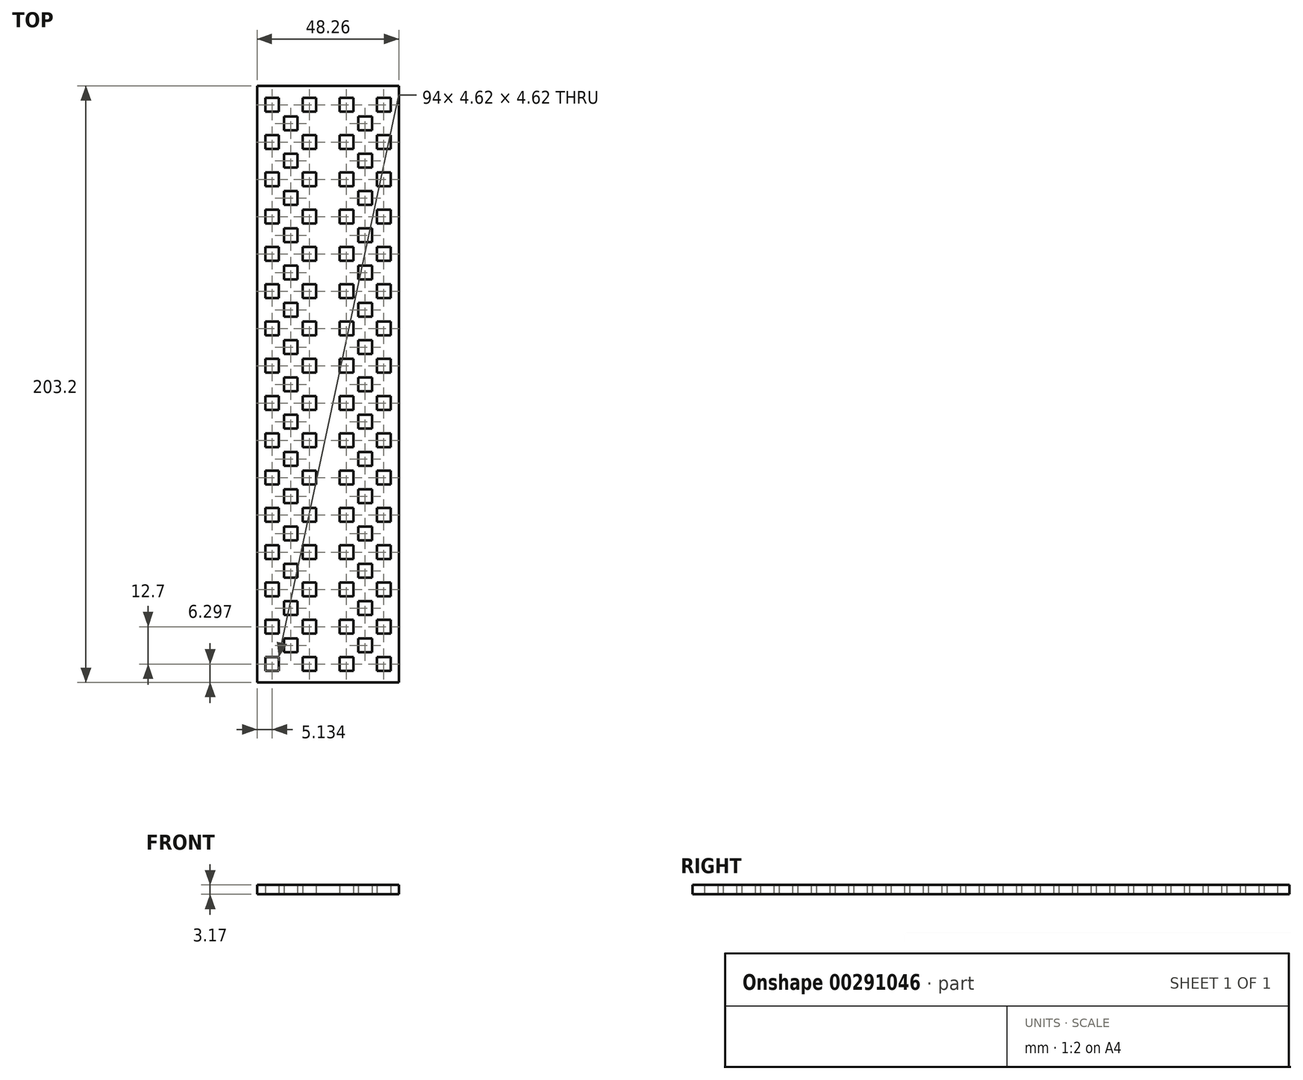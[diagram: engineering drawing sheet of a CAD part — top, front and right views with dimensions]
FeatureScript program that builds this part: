
annotation { "Feature Type Name" : "Feature", "Feature Type Description" : "" }
export const myFeature = defineFeature(function(context is Context, id is Id, definition is map)
    precondition{}
    {
        {
            var Q0;
            Q0=qCreatedBy(makeId("Top.planeOp"),FACE);
            var sketch = newSketch(context, id + "F0", { "sketchPlane" : qUnion([Q0])});
            skLineSegment(sketch, "E0.bottom", {"start": v(-11.58, 137.79) * mm, "end": v(12.55, 137.79) * mm});
            skLineSegment(sketch, "E0.top", {"start": v(-11.58, -65.41) * mm, "end": v(12.55, -65.41) * mm});
            skLineSegment(sketch, "E0.left", {"start": v(-11.58, 137.79) * mm, "end": v(-11.58, -65.41) * mm});
            skLineSegment(sketch, "E0.right", {"start": v(12.55, 137.79) * mm, "end": v(12.55, -65.41) * mm});
            skPoint(sketch, "E1", {"position": v(-7.59, 137.79) * mm});
            skPoint(sketch, "E2", {"position": v(-11.58, 133.7) * mm});
            skLineSegment(sketch, "E3.bottom", {"start": v(-7.59, 133.7) * mm, "end": v(-2.97, 133.7) * mm});
            skLineSegment(sketch, "E3.top", {"start": v(-7.59, 129.08) * mm, "end": v(-2.97, 129.08) * mm});
            skLineSegment(sketch, "E3.left", {"start": v(-7.59, 133.7) * mm, "end": v(-7.59, 129.08) * mm});
            skLineSegment(sketch, "E3.right", {"start": v(-2.97, 133.7) * mm, "end": v(-2.97, 129.08) * mm});
            skPoint(sketch, "E4", {"position": v(-5.28, 133.7) * mm});
            skPoint(sketch, "E5", {"position": v(-7.59, 131.39) * mm});
            skPoint(sketch, "E6", {"position": v(7.42, 133.7) * mm});
            skPoint(sketch, "E7", {"position": v(1.07, 133.7) * mm});
            skLineSegment(sketch, "E8.bottom", {"start": v(5.11, 133.7) * mm, "end": v(9.73, 133.7) * mm});
            skLineSegment(sketch, "E8.top", {"start": v(5.11, 129.08) * mm, "end": v(9.73, 129.08) * mm});
            skLineSegment(sketch, "E8.left", {"start": v(5.11, 133.7) * mm, "end": v(5.11, 129.08) * mm});
            skLineSegment(sketch, "E8.right", {"start": v(9.73, 133.7) * mm, "end": v(9.73, 129.08) * mm});
            skPoint(sketch, "E9", {"position": v(-7.59, 118.84) * mm});
            skPoint(sketch, "E10.0.1.0", {"position": v(7.42, 121) * mm});
            skPoint(sketch, "E10.0.1.1", {"position": v(-7.59, 118.69) * mm});
            skLineSegment(sketch, "E10.0.1.2", {"start": v(9.73, 121) * mm, "end": v(9.73, 116.38) * mm});
            skLineSegment(sketch, "E10.0.1.3", {"start": v(5.11, 121) * mm, "end": v(5.11, 116.38) * mm});
            skLineSegment(sketch, "E10.0.1.4", {"start": v(5.11, 116.38) * mm, "end": v(9.73, 116.38) * mm});
            skLineSegment(sketch, "E10.0.1.5", {"start": v(-2.97, 121) * mm, "end": v(-2.97, 116.38) * mm});
            skLineSegment(sketch, "E10.0.1.6", {"start": v(-7.59, 116.38) * mm, "end": v(-2.97, 116.38) * mm});
            skPoint(sketch, "E10.0.1.7", {"position": v(1.07, 121) * mm});
            skPoint(sketch, "E10.0.1.8", {"position": v(-5.28, 121) * mm});
            skLineSegment(sketch, "E10.0.1.9", {"start": v(5.11, 121) * mm, "end": v(9.73, 121) * mm});
            skLineSegment(sketch, "E10.0.1.10", {"start": v(-7.59, 121) * mm, "end": v(-7.59, 116.38) * mm});
            skLineSegment(sketch, "E10.0.1.11", {"start": v(-7.59, 121) * mm, "end": v(-2.97, 121) * mm});
            skPoint(sketch, "E10.0.2.0", {"position": v(7.42, 108.3) * mm});
            skPoint(sketch, "E10.0.2.1", {"position": v(-7.59, 105.99) * mm});
            skLineSegment(sketch, "E10.0.2.2", {"start": v(9.73, 108.3) * mm, "end": v(9.73, 103.68) * mm});
            skLineSegment(sketch, "E10.0.2.3", {"start": v(5.11, 108.3) * mm, "end": v(5.11, 103.68) * mm});
            skLineSegment(sketch, "E10.0.2.4", {"start": v(5.11, 103.68) * mm, "end": v(9.73, 103.68) * mm});
            skLineSegment(sketch, "E10.0.2.5", {"start": v(-2.97, 108.3) * mm, "end": v(-2.97, 103.68) * mm});
            skLineSegment(sketch, "E10.0.2.6", {"start": v(-7.59, 103.68) * mm, "end": v(-2.97, 103.68) * mm});
            skPoint(sketch, "E10.0.2.7", {"position": v(1.07, 108.3) * mm});
            skPoint(sketch, "E10.0.2.8", {"position": v(-5.28, 108.3) * mm});
            skLineSegment(sketch, "E10.0.2.9", {"start": v(5.11, 108.3) * mm, "end": v(9.73, 108.3) * mm});
            skLineSegment(sketch, "E10.0.2.10", {"start": v(-7.59, 108.3) * mm, "end": v(-7.59, 103.68) * mm});
            skLineSegment(sketch, "E10.0.2.11", {"start": v(-7.59, 108.3) * mm, "end": v(-2.97, 108.3) * mm});
            skPoint(sketch, "E10.0.3.0", {"position": v(7.42, 95.6) * mm});
            skPoint(sketch, "E10.0.3.1", {"position": v(-7.59, 93.29) * mm});
            skLineSegment(sketch, "E10.0.3.2", {"start": v(9.73, 95.6) * mm, "end": v(9.73, 90.98) * mm});
            skLineSegment(sketch, "E10.0.3.3", {"start": v(5.11, 95.6) * mm, "end": v(5.11, 90.98) * mm});
            skLineSegment(sketch, "E10.0.3.4", {"start": v(5.11, 90.98) * mm, "end": v(9.73, 90.98) * mm});
            skLineSegment(sketch, "E10.0.3.5", {"start": v(-2.97, 95.6) * mm, "end": v(-2.97, 90.98) * mm});
            skLineSegment(sketch, "E10.0.3.6", {"start": v(-7.59, 90.98) * mm, "end": v(-2.97, 90.98) * mm});
            skPoint(sketch, "E10.0.3.7", {"position": v(1.07, 95.6) * mm});
            skPoint(sketch, "E10.0.3.8", {"position": v(-5.28, 95.6) * mm});
            skLineSegment(sketch, "E10.0.3.9", {"start": v(5.11, 95.6) * mm, "end": v(9.73, 95.6) * mm});
            skLineSegment(sketch, "E10.0.3.10", {"start": v(-7.59, 95.6) * mm, "end": v(-7.59, 90.98) * mm});
            skLineSegment(sketch, "E10.0.3.11", {"start": v(-7.59, 95.6) * mm, "end": v(-2.97, 95.6) * mm});
            skPoint(sketch, "E10.0.4.0", {"position": v(7.42, 82.9) * mm});
            skPoint(sketch, "E10.0.4.1", {"position": v(-7.59, 80.59) * mm});
            skLineSegment(sketch, "E10.0.4.2", {"start": v(9.73, 82.9) * mm, "end": v(9.73, 78.28) * mm});
            skLineSegment(sketch, "E10.0.4.3", {"start": v(5.11, 82.9) * mm, "end": v(5.11, 78.28) * mm});
            skLineSegment(sketch, "E10.0.4.4", {"start": v(5.11, 78.28) * mm, "end": v(9.73, 78.28) * mm});
            skLineSegment(sketch, "E10.0.4.5", {"start": v(-2.97, 82.9) * mm, "end": v(-2.97, 78.28) * mm});
            skLineSegment(sketch, "E10.0.4.6", {"start": v(-7.59, 78.28) * mm, "end": v(-2.97, 78.28) * mm});
            skPoint(sketch, "E10.0.4.7", {"position": v(1.07, 82.9) * mm});
            skPoint(sketch, "E10.0.4.8", {"position": v(-5.28, 82.9) * mm});
            skLineSegment(sketch, "E10.0.4.9", {"start": v(5.11, 82.9) * mm, "end": v(9.73, 82.9) * mm});
            skLineSegment(sketch, "E10.0.4.10", {"start": v(-7.59, 82.9) * mm, "end": v(-7.59, 78.28) * mm});
            skLineSegment(sketch, "E10.0.4.11", {"start": v(-7.59, 82.9) * mm, "end": v(-2.97, 82.9) * mm});
            skPoint(sketch, "E10.0.5.0", {"position": v(7.42, 70.2) * mm});
            skPoint(sketch, "E10.0.5.1", {"position": v(-7.59, 67.89) * mm});
            skLineSegment(sketch, "E10.0.5.2", {"start": v(9.73, 70.2) * mm, "end": v(9.73, 65.58) * mm});
            skLineSegment(sketch, "E10.0.5.3", {"start": v(5.11, 70.2) * mm, "end": v(5.11, 65.58) * mm});
            skLineSegment(sketch, "E10.0.5.4", {"start": v(5.11, 65.58) * mm, "end": v(9.73, 65.58) * mm});
            skLineSegment(sketch, "E10.0.5.5", {"start": v(-2.97, 70.2) * mm, "end": v(-2.97, 65.58) * mm});
            skLineSegment(sketch, "E10.0.5.6", {"start": v(-7.59, 65.58) * mm, "end": v(-2.97, 65.58) * mm});
            skPoint(sketch, "E10.0.5.7", {"position": v(1.07, 70.2) * mm});
            skPoint(sketch, "E10.0.5.8", {"position": v(-5.28, 70.2) * mm});
            skLineSegment(sketch, "E10.0.5.9", {"start": v(5.11, 70.2) * mm, "end": v(9.73, 70.2) * mm});
            skLineSegment(sketch, "E10.0.5.10", {"start": v(-7.59, 70.2) * mm, "end": v(-7.59, 65.58) * mm});
            skLineSegment(sketch, "E10.0.5.11", {"start": v(-7.59, 70.2) * mm, "end": v(-2.97, 70.2) * mm});
            skPoint(sketch, "E10.0.6.0", {"position": v(7.42, 57.5) * mm});
            skPoint(sketch, "E10.0.6.1", {"position": v(-7.59, 55.19) * mm});
            skLineSegment(sketch, "E10.0.6.2", {"start": v(9.73, 57.5) * mm, "end": v(9.73, 52.88) * mm});
            skLineSegment(sketch, "E10.0.6.3", {"start": v(5.11, 57.5) * mm, "end": v(5.11, 52.88) * mm});
            skLineSegment(sketch, "E10.0.6.4", {"start": v(5.11, 52.88) * mm, "end": v(9.73, 52.88) * mm});
            skLineSegment(sketch, "E10.0.6.5", {"start": v(-2.97, 57.5) * mm, "end": v(-2.97, 52.88) * mm});
            skLineSegment(sketch, "E10.0.6.6", {"start": v(-7.59, 52.88) * mm, "end": v(-2.97, 52.88) * mm});
            skPoint(sketch, "E10.0.6.7", {"position": v(1.07, 57.5) * mm});
            skPoint(sketch, "E10.0.6.8", {"position": v(-5.28, 57.5) * mm});
            skLineSegment(sketch, "E10.0.6.9", {"start": v(5.11, 57.5) * mm, "end": v(9.73, 57.5) * mm});
            skLineSegment(sketch, "E10.0.6.10", {"start": v(-7.59, 57.5) * mm, "end": v(-7.59, 52.88) * mm});
            skLineSegment(sketch, "E10.0.6.11", {"start": v(-7.59, 57.5) * mm, "end": v(-2.97, 57.5) * mm});
            skPoint(sketch, "E10.0.7.0", {"position": v(7.42, 44.8) * mm});
            skPoint(sketch, "E10.0.7.1", {"position": v(-7.59, 42.49) * mm});
            skLineSegment(sketch, "E10.0.7.2", {"start": v(9.73, 44.8) * mm, "end": v(9.73, 40.18) * mm});
            skLineSegment(sketch, "E10.0.7.3", {"start": v(5.11, 44.8) * mm, "end": v(5.11, 40.18) * mm});
            skLineSegment(sketch, "E10.0.7.4", {"start": v(5.11, 40.18) * mm, "end": v(9.73, 40.18) * mm});
            skLineSegment(sketch, "E10.0.7.5", {"start": v(-2.97, 44.8) * mm, "end": v(-2.97, 40.18) * mm});
            skLineSegment(sketch, "E10.0.7.6", {"start": v(-7.59, 40.18) * mm, "end": v(-2.97, 40.18) * mm});
            skPoint(sketch, "E10.0.7.7", {"position": v(1.07, 44.8) * mm});
            skPoint(sketch, "E10.0.7.8", {"position": v(-5.28, 44.8) * mm});
            skLineSegment(sketch, "E10.0.7.9", {"start": v(5.11, 44.8) * mm, "end": v(9.73, 44.8) * mm});
            skLineSegment(sketch, "E10.0.7.10", {"start": v(-7.59, 44.8) * mm, "end": v(-7.59, 40.18) * mm});
            skLineSegment(sketch, "E10.0.7.11", {"start": v(-7.59, 44.8) * mm, "end": v(-2.97, 44.8) * mm});
            skPoint(sketch, "E10.0.8.0", {"position": v(7.42, 32.1) * mm});
            skPoint(sketch, "E10.0.8.1", {"position": v(-7.59, 29.79) * mm});
            skLineSegment(sketch, "E10.0.8.2", {"start": v(9.73, 32.1) * mm, "end": v(9.73, 27.48) * mm});
            skLineSegment(sketch, "E10.0.8.3", {"start": v(5.11, 32.1) * mm, "end": v(5.11, 27.48) * mm});
            skLineSegment(sketch, "E10.0.8.4", {"start": v(5.11, 27.48) * mm, "end": v(9.73, 27.48) * mm});
            skLineSegment(sketch, "E10.0.8.5", {"start": v(-2.97, 32.1) * mm, "end": v(-2.97, 27.48) * mm});
            skLineSegment(sketch, "E10.0.8.6", {"start": v(-7.59, 27.48) * mm, "end": v(-2.97, 27.48) * mm});
            skPoint(sketch, "E10.0.8.7", {"position": v(1.07, 32.1) * mm});
            skPoint(sketch, "E10.0.8.8", {"position": v(-5.28, 32.1) * mm});
            skLineSegment(sketch, "E10.0.8.9", {"start": v(5.11, 32.1) * mm, "end": v(9.73, 32.1) * mm});
            skLineSegment(sketch, "E10.0.8.10", {"start": v(-7.59, 32.1) * mm, "end": v(-7.59, 27.48) * mm});
            skLineSegment(sketch, "E10.0.8.11", {"start": v(-7.59, 32.1) * mm, "end": v(-2.97, 32.1) * mm});
            skPoint(sketch, "E10.0.9.0", {"position": v(7.42, 19.4) * mm});
            skPoint(sketch, "E10.0.9.1", {"position": v(-7.59, 17.09) * mm});
            skLineSegment(sketch, "E10.0.9.2", {"start": v(9.73, 19.4) * mm, "end": v(9.73, 14.78) * mm});
            skLineSegment(sketch, "E10.0.9.3", {"start": v(5.11, 19.4) * mm, "end": v(5.11, 14.78) * mm});
            skLineSegment(sketch, "E10.0.9.4", {"start": v(5.11, 14.78) * mm, "end": v(9.73, 14.78) * mm});
            skLineSegment(sketch, "E10.0.9.5", {"start": v(-2.97, 19.4) * mm, "end": v(-2.97, 14.78) * mm});
            skLineSegment(sketch, "E10.0.9.6", {"start": v(-7.59, 14.78) * mm, "end": v(-2.97, 14.78) * mm});
            skPoint(sketch, "E10.0.9.7", {"position": v(1.07, 19.4) * mm});
            skPoint(sketch, "E10.0.9.8", {"position": v(-5.28, 19.4) * mm});
            skLineSegment(sketch, "E10.0.9.9", {"start": v(5.11, 19.4) * mm, "end": v(9.73, 19.4) * mm});
            skLineSegment(sketch, "E10.0.9.10", {"start": v(-7.59, 19.4) * mm, "end": v(-7.59, 14.78) * mm});
            skLineSegment(sketch, "E10.0.9.11", {"start": v(-7.59, 19.4) * mm, "end": v(-2.97, 19.4) * mm});
            skPoint(sketch, "E10.0.10.0", {"position": v(7.42, 6.7) * mm});
            skPoint(sketch, "E10.0.10.1", {"position": v(-7.59, 4.39) * mm});
            skLineSegment(sketch, "E10.0.10.2", {"start": v(9.73, 6.7) * mm, "end": v(9.73, 2.08) * mm});
            skLineSegment(sketch, "E10.0.10.3", {"start": v(5.11, 6.7) * mm, "end": v(5.11, 2.08) * mm});
            skLineSegment(sketch, "E10.0.10.4", {"start": v(5.11, 2.08) * mm, "end": v(9.73, 2.08) * mm});
            skLineSegment(sketch, "E10.0.10.5", {"start": v(-2.97, 6.7) * mm, "end": v(-2.97, 2.08) * mm});
            skLineSegment(sketch, "E10.0.10.6", {"start": v(-7.59, 2.08) * mm, "end": v(-2.97, 2.08) * mm});
            skPoint(sketch, "E10.0.10.7", {"position": v(1.07, 6.7) * mm});
            skPoint(sketch, "E10.0.10.8", {"position": v(-5.28, 6.7) * mm});
            skLineSegment(sketch, "E10.0.10.9", {"start": v(5.11, 6.7) * mm, "end": v(9.73, 6.7) * mm});
            skLineSegment(sketch, "E10.0.10.10", {"start": v(-7.59, 6.7) * mm, "end": v(-7.59, 2.08) * mm});
            skLineSegment(sketch, "E10.0.10.11", {"start": v(-7.59, 6.7) * mm, "end": v(-2.97, 6.7) * mm});
            skPoint(sketch, "E10.0.11.0", {"position": v(7.42, -6) * mm});
            skPoint(sketch, "E10.0.11.1", {"position": v(-7.59, -8.31) * mm});
            skLineSegment(sketch, "E10.0.11.2", {"start": v(9.73, -6) * mm, "end": v(9.73, -10.62) * mm});
            skLineSegment(sketch, "E10.0.11.3", {"start": v(5.11, -6) * mm, "end": v(5.11, -10.62) * mm});
            skLineSegment(sketch, "E10.0.11.4", {"start": v(5.11, -10.62) * mm, "end": v(9.73, -10.62) * mm});
            skLineSegment(sketch, "E10.0.11.5", {"start": v(-2.97, -6) * mm, "end": v(-2.97, -10.62) * mm});
            skLineSegment(sketch, "E10.0.11.6", {"start": v(-7.59, -10.62) * mm, "end": v(-2.97, -10.62) * mm});
            skPoint(sketch, "E10.0.11.7", {"position": v(1.07, -6) * mm});
            skPoint(sketch, "E10.0.11.8", {"position": v(-5.28, -6) * mm});
            skLineSegment(sketch, "E10.0.11.9", {"start": v(5.11, -6) * mm, "end": v(9.73, -6) * mm});
            skLineSegment(sketch, "E10.0.11.10", {"start": v(-7.59, -6) * mm, "end": v(-7.59, -10.62) * mm});
            skLineSegment(sketch, "E10.0.11.11", {"start": v(-7.59, -6) * mm, "end": v(-2.97, -6) * mm});
            skPoint(sketch, "E10.0.12.0", {"position": v(7.42, -18.7) * mm});
            skPoint(sketch, "E10.0.12.1", {"position": v(-7.59, -21.01) * mm});
            skLineSegment(sketch, "E10.0.12.2", {"start": v(9.73, -18.7) * mm, "end": v(9.73, -23.32) * mm});
            skLineSegment(sketch, "E10.0.12.3", {"start": v(5.11, -18.7) * mm, "end": v(5.11, -23.32) * mm});
            skLineSegment(sketch, "E10.0.12.4", {"start": v(5.11, -23.32) * mm, "end": v(9.73, -23.32) * mm});
            skLineSegment(sketch, "E10.0.12.5", {"start": v(-2.97, -18.7) * mm, "end": v(-2.97, -23.32) * mm});
            skLineSegment(sketch, "E10.0.12.6", {"start": v(-7.59, -23.32) * mm, "end": v(-2.97, -23.32) * mm});
            skPoint(sketch, "E10.0.12.7", {"position": v(1.07, -18.7) * mm});
            skPoint(sketch, "E10.0.12.8", {"position": v(-5.28, -18.7) * mm});
            skLineSegment(sketch, "E10.0.12.9", {"start": v(5.11, -18.7) * mm, "end": v(9.73, -18.7) * mm});
            skLineSegment(sketch, "E10.0.12.10", {"start": v(-7.59, -18.7) * mm, "end": v(-7.59, -23.32) * mm});
            skLineSegment(sketch, "E10.0.12.11", {"start": v(-7.59, -18.7) * mm, "end": v(-2.97, -18.7) * mm});
            skPoint(sketch, "E10.0.13.0", {"position": v(7.42, -31.4) * mm});
            skPoint(sketch, "E10.0.13.1", {"position": v(-7.59, -33.71) * mm});
            skLineSegment(sketch, "E10.0.13.2", {"start": v(9.73, -31.4) * mm, "end": v(9.73, -36.02) * mm});
            skLineSegment(sketch, "E10.0.13.3", {"start": v(5.11, -31.4) * mm, "end": v(5.11, -36.02) * mm});
            skLineSegment(sketch, "E10.0.13.4", {"start": v(5.11, -36.02) * mm, "end": v(9.73, -36.02) * mm});
            skLineSegment(sketch, "E10.0.13.5", {"start": v(-2.97, -31.4) * mm, "end": v(-2.97, -36.02) * mm});
            skLineSegment(sketch, "E10.0.13.6", {"start": v(-7.59, -36.02) * mm, "end": v(-2.97, -36.02) * mm});
            skPoint(sketch, "E10.0.13.7", {"position": v(1.07, -31.4) * mm});
            skPoint(sketch, "E10.0.13.8", {"position": v(-5.28, -31.4) * mm});
            skLineSegment(sketch, "E10.0.13.9", {"start": v(5.11, -31.4) * mm, "end": v(9.73, -31.4) * mm});
            skLineSegment(sketch, "E10.0.13.10", {"start": v(-7.59, -31.4) * mm, "end": v(-7.59, -36.02) * mm});
            skLineSegment(sketch, "E10.0.13.11", {"start": v(-7.59, -31.4) * mm, "end": v(-2.97, -31.4) * mm});
            skPoint(sketch, "E10.0.14.0", {"position": v(7.42, -44.1) * mm});
            skPoint(sketch, "E10.0.14.1", {"position": v(-7.59, -46.41) * mm});
            skLineSegment(sketch, "E10.0.14.2", {"start": v(9.73, -44.1) * mm, "end": v(9.73, -48.72) * mm});
            skLineSegment(sketch, "E10.0.14.3", {"start": v(5.11, -44.1) * mm, "end": v(5.11, -48.72) * mm});
            skLineSegment(sketch, "E10.0.14.4", {"start": v(5.11, -48.72) * mm, "end": v(9.73, -48.72) * mm});
            skLineSegment(sketch, "E10.0.14.5", {"start": v(-2.97, -44.1) * mm, "end": v(-2.97, -48.72) * mm});
            skLineSegment(sketch, "E10.0.14.6", {"start": v(-7.59, -48.72) * mm, "end": v(-2.97, -48.72) * mm});
            skPoint(sketch, "E10.0.14.7", {"position": v(1.07, -44.1) * mm});
            skPoint(sketch, "E10.0.14.8", {"position": v(-5.28, -44.1) * mm});
            skLineSegment(sketch, "E10.0.14.9", {"start": v(5.11, -44.1) * mm, "end": v(9.73, -44.1) * mm});
            skLineSegment(sketch, "E10.0.14.10", {"start": v(-7.59, -44.1) * mm, "end": v(-7.59, -48.72) * mm});
            skLineSegment(sketch, "E10.0.14.11", {"start": v(-7.59, -44.1) * mm, "end": v(-2.97, -44.1) * mm});
            skPoint(sketch, "E10.0.15.0", {"position": v(7.42, -56.8) * mm});
            skPoint(sketch, "E10.0.15.1", {"position": v(-7.59, -59.11) * mm});
            skLineSegment(sketch, "E10.0.15.2", {"start": v(9.73, -56.8) * mm, "end": v(9.73, -61.42) * mm});
            skLineSegment(sketch, "E10.0.15.3", {"start": v(5.11, -56.8) * mm, "end": v(5.11, -61.42) * mm});
            skLineSegment(sketch, "E10.0.15.4", {"start": v(5.11, -61.42) * mm, "end": v(9.73, -61.42) * mm});
            skLineSegment(sketch, "E10.0.15.5", {"start": v(-2.97, -56.8) * mm, "end": v(-2.97, -61.42) * mm});
            skLineSegment(sketch, "E10.0.15.6", {"start": v(-7.59, -61.42) * mm, "end": v(-2.97, -61.42) * mm});
            skPoint(sketch, "E10.0.15.7", {"position": v(1.07, -56.8) * mm});
            skPoint(sketch, "E10.0.15.8", {"position": v(-5.28, -56.8) * mm});
            skLineSegment(sketch, "E10.0.15.9", {"start": v(5.11, -56.8) * mm, "end": v(9.73, -56.8) * mm});
            skLineSegment(sketch, "E10.0.15.10", {"start": v(-7.59, -56.8) * mm, "end": v(-7.59, -61.42) * mm});
            skLineSegment(sketch, "E10.0.15.11", {"start": v(-7.59, -56.8) * mm, "end": v(-2.97, -56.8) * mm});
            skLineSegment(sketch, "E10.direction1", {"start": v(-7.59, 131.39) * mm, "end": v(17.81, 131.39) * mm, "construction": true});
            skLineSegment(sketch, "E10.direction2", {"start": v(-7.59, 131.39) * mm, "end": v(-7.59, 118.69) * mm, "construction": true});
            skPoint(sketch, "E11", {"position": v(1.07, 127.35) * mm});
            skLineSegment(sketch, "E12.bottom", {"start": v(-1.24, 127.35) * mm, "end": v(3.38, 127.35) * mm});
            skLineSegment(sketch, "E12.top", {"start": v(-1.24, 122.73) * mm, "end": v(3.38, 122.73) * mm});
            skLineSegment(sketch, "E12.left", {"start": v(-1.24, 127.35) * mm, "end": v(-1.24, 122.73) * mm});
            skLineSegment(sketch, "E12.right", {"start": v(3.38, 127.35) * mm, "end": v(3.38, 122.73) * mm});
            skLineSegment(sketch, "E13.0.1.0", {"start": v(3.38, 114.65) * mm, "end": v(3.38, 110.03) * mm});
            skLineSegment(sketch, "E13.0.1.1", {"start": v(-1.24, 114.65) * mm, "end": v(-1.24, 110.03) * mm});
            skLineSegment(sketch, "E13.0.1.2", {"start": v(-1.24, 110.03) * mm, "end": v(3.38, 110.03) * mm});
            skPoint(sketch, "E13.0.1.3", {"position": v(1.07, 114.65) * mm});
            skLineSegment(sketch, "E13.0.1.4", {"start": v(-1.24, 114.65) * mm, "end": v(3.38, 114.65) * mm});
            skLineSegment(sketch, "E13.0.2.0", {"start": v(3.38, 101.95) * mm, "end": v(3.38, 97.33) * mm});
            skLineSegment(sketch, "E13.0.2.1", {"start": v(-1.24, 101.95) * mm, "end": v(-1.24, 97.33) * mm});
            skLineSegment(sketch, "E13.0.2.2", {"start": v(-1.24, 97.33) * mm, "end": v(3.38, 97.33) * mm});
            skPoint(sketch, "E13.0.2.3", {"position": v(1.07, 101.95) * mm});
            skLineSegment(sketch, "E13.0.2.4", {"start": v(-1.24, 101.95) * mm, "end": v(3.38, 101.95) * mm});
            skLineSegment(sketch, "E13.0.3.0", {"start": v(3.38, 89.25) * mm, "end": v(3.38, 84.63) * mm});
            skLineSegment(sketch, "E13.0.3.1", {"start": v(-1.24, 89.25) * mm, "end": v(-1.24, 84.63) * mm});
            skLineSegment(sketch, "E13.0.3.2", {"start": v(-1.24, 84.63) * mm, "end": v(3.38, 84.63) * mm});
            skPoint(sketch, "E13.0.3.3", {"position": v(1.07, 89.25) * mm});
            skLineSegment(sketch, "E13.0.3.4", {"start": v(-1.24, 89.25) * mm, "end": v(3.38, 89.25) * mm});
            skLineSegment(sketch, "E13.0.4.0", {"start": v(3.38, 76.55) * mm, "end": v(3.38, 71.93) * mm});
            skLineSegment(sketch, "E13.0.4.1", {"start": v(-1.24, 76.55) * mm, "end": v(-1.24, 71.93) * mm});
            skLineSegment(sketch, "E13.0.4.2", {"start": v(-1.24, 71.93) * mm, "end": v(3.38, 71.93) * mm});
            skPoint(sketch, "E13.0.4.3", {"position": v(1.07, 76.55) * mm});
            skLineSegment(sketch, "E13.0.4.4", {"start": v(-1.24, 76.55) * mm, "end": v(3.38, 76.55) * mm});
            skLineSegment(sketch, "E13.0.5.0", {"start": v(3.38, 63.85) * mm, "end": v(3.38, 59.23) * mm});
            skLineSegment(sketch, "E13.0.5.1", {"start": v(-1.24, 63.85) * mm, "end": v(-1.24, 59.23) * mm});
            skLineSegment(sketch, "E13.0.5.2", {"start": v(-1.24, 59.23) * mm, "end": v(3.38, 59.23) * mm});
            skPoint(sketch, "E13.0.5.3", {"position": v(1.07, 63.85) * mm});
            skLineSegment(sketch, "E13.0.5.4", {"start": v(-1.24, 63.85) * mm, "end": v(3.38, 63.85) * mm});
            skLineSegment(sketch, "E13.0.6.0", {"start": v(3.38, 51.15) * mm, "end": v(3.38, 46.53) * mm});
            skLineSegment(sketch, "E13.0.6.1", {"start": v(-1.24, 51.15) * mm, "end": v(-1.24, 46.53) * mm});
            skLineSegment(sketch, "E13.0.6.2", {"start": v(-1.24, 46.53) * mm, "end": v(3.38, 46.53) * mm});
            skPoint(sketch, "E13.0.6.3", {"position": v(1.07, 51.15) * mm});
            skLineSegment(sketch, "E13.0.6.4", {"start": v(-1.24, 51.15) * mm, "end": v(3.38, 51.15) * mm});
            skLineSegment(sketch, "E13.0.7.0", {"start": v(3.38, 38.45) * mm, "end": v(3.38, 33.83) * mm});
            skLineSegment(sketch, "E13.0.7.1", {"start": v(-1.24, 38.45) * mm, "end": v(-1.24, 33.83) * mm});
            skLineSegment(sketch, "E13.0.7.2", {"start": v(-1.24, 33.83) * mm, "end": v(3.38, 33.83) * mm});
            skPoint(sketch, "E13.0.7.3", {"position": v(1.07, 38.45) * mm});
            skLineSegment(sketch, "E13.0.7.4", {"start": v(-1.24, 38.45) * mm, "end": v(3.38, 38.45) * mm});
            skLineSegment(sketch, "E13.0.8.0", {"start": v(3.38, 25.75) * mm, "end": v(3.38, 21.13) * mm});
            skLineSegment(sketch, "E13.0.8.1", {"start": v(-1.24, 25.75) * mm, "end": v(-1.24, 21.13) * mm});
            skLineSegment(sketch, "E13.0.8.2", {"start": v(-1.24, 21.13) * mm, "end": v(3.38, 21.13) * mm});
            skPoint(sketch, "E13.0.8.3", {"position": v(1.07, 25.75) * mm});
            skLineSegment(sketch, "E13.0.8.4", {"start": v(-1.24, 25.75) * mm, "end": v(3.38, 25.75) * mm});
            skLineSegment(sketch, "E13.0.9.0", {"start": v(3.38, 13.05) * mm, "end": v(3.38, 8.43) * mm});
            skLineSegment(sketch, "E13.0.9.1", {"start": v(-1.24, 13.05) * mm, "end": v(-1.24, 8.43) * mm});
            skLineSegment(sketch, "E13.0.9.2", {"start": v(-1.24, 8.43) * mm, "end": v(3.38, 8.43) * mm});
            skPoint(sketch, "E13.0.9.3", {"position": v(1.07, 13.05) * mm});
            skLineSegment(sketch, "E13.0.9.4", {"start": v(-1.24, 13.05) * mm, "end": v(3.38, 13.05) * mm});
            skLineSegment(sketch, "E13.0.10.0", {"start": v(3.38, 0.35) * mm, "end": v(3.38, -4.27) * mm});
            skLineSegment(sketch, "E13.0.10.1", {"start": v(-1.24, 0.35) * mm, "end": v(-1.24, -4.27) * mm});
            skLineSegment(sketch, "E13.0.10.2", {"start": v(-1.24, -4.27) * mm, "end": v(3.38, -4.27) * mm});
            skPoint(sketch, "E13.0.10.3", {"position": v(1.07, 0.35) * mm});
            skLineSegment(sketch, "E13.0.10.4", {"start": v(-1.24, 0.35) * mm, "end": v(3.38, 0.35) * mm});
            skLineSegment(sketch, "E13.0.11.0", {"start": v(3.38, -12.35) * mm, "end": v(3.38, -16.97) * mm});
            skLineSegment(sketch, "E13.0.11.1", {"start": v(-1.24, -12.35) * mm, "end": v(-1.24, -16.97) * mm});
            skLineSegment(sketch, "E13.0.11.2", {"start": v(-1.24, -16.97) * mm, "end": v(3.38, -16.97) * mm});
            skPoint(sketch, "E13.0.11.3", {"position": v(1.07, -12.35) * mm});
            skLineSegment(sketch, "E13.0.11.4", {"start": v(-1.24, -12.35) * mm, "end": v(3.38, -12.35) * mm});
            skLineSegment(sketch, "E13.0.12.0", {"start": v(3.38, -25.05) * mm, "end": v(3.38, -29.67) * mm});
            skLineSegment(sketch, "E13.0.12.1", {"start": v(-1.24, -25.05) * mm, "end": v(-1.24, -29.67) * mm});
            skLineSegment(sketch, "E13.0.12.2", {"start": v(-1.24, -29.67) * mm, "end": v(3.38, -29.67) * mm});
            skPoint(sketch, "E13.0.12.3", {"position": v(1.07, -25.05) * mm});
            skLineSegment(sketch, "E13.0.12.4", {"start": v(-1.24, -25.05) * mm, "end": v(3.38, -25.05) * mm});
            skLineSegment(sketch, "E13.0.13.0", {"start": v(3.38, -37.75) * mm, "end": v(3.38, -42.37) * mm});
            skLineSegment(sketch, "E13.0.13.1", {"start": v(-1.24, -37.75) * mm, "end": v(-1.24, -42.37) * mm});
            skLineSegment(sketch, "E13.0.13.2", {"start": v(-1.24, -42.37) * mm, "end": v(3.38, -42.37) * mm});
            skPoint(sketch, "E13.0.13.3", {"position": v(1.07, -37.75) * mm});
            skLineSegment(sketch, "E13.0.13.4", {"start": v(-1.24, -37.75) * mm, "end": v(3.38, -37.75) * mm});
            skLineSegment(sketch, "E13.0.14.0", {"start": v(3.38, -50.45) * mm, "end": v(3.38, -55.07) * mm});
            skLineSegment(sketch, "E13.0.14.1", {"start": v(-1.24, -50.45) * mm, "end": v(-1.24, -55.07) * mm});
            skLineSegment(sketch, "E13.0.14.2", {"start": v(-1.24, -55.07) * mm, "end": v(3.38, -55.07) * mm});
            skPoint(sketch, "E13.0.14.3", {"position": v(1.07, -50.45) * mm});
            skLineSegment(sketch, "E13.0.14.4", {"start": v(-1.24, -50.45) * mm, "end": v(3.38, -50.45) * mm});
            skLineSegment(sketch, "E13.direction1", {"start": v(-1.24, 122.73) * mm, "end": v(24.16, 122.73) * mm, "construction": true});
            skLineSegment(sketch, "E13.direction2", {"start": v(-1.24, 122.73) * mm, "end": v(-1.24, 110.03) * mm, "construction": true});
            skSolve(sketch);
        }
        {
            var Q0;
            Q0=makeQuery(id+"F0.imprint","IMPRINT",FACE,{"disambiguationData":[TD([[makeQuery(id+"F0.imprint","IMPRINT",EDGE,{"derivedFrom":sQuery(id+"F0.wireOp",EDGE,"E0.bottom")}),-1.0]])]});
            extrude(context, id + "F1", {"entities" : qUnion([Q0]), "depth" : 3.17 * mm});
        }
        {
            var Q0;
            Q0=makeQuery(id+"F1.opExtrude","SWEPT_BODY",BODY,{"disambiguationData":[OSD([sQuery(id+"F0.wireOp",EDGE,"E0.bottom"),sQuery(id+"F0.wireOp",EDGE,"E0.top"),sQuery(id+"F0.wireOp",EDGE,"E0.left"),sQuery(id+"F0.wireOp",EDGE,"E0.right"),sQuery(id+"F0.wireOp",EDGE,"E3.bottom"),sQuery(id+"F0.wireOp",EDGE,"E3.top"),sQuery(id+"F0.wireOp",EDGE,"E3.left"),sQuery(id+"F0.wireOp",EDGE,"E3.right"),sQuery(id+"F0.wireOp",EDGE,"E8.bottom"),sQuery(id+"F0.wireOp",EDGE,"E8.top"),sQuery(id+"F0.wireOp",EDGE,"E8.left"),sQuery(id+"F0.wireOp",EDGE,"E8.right"),sQuery(id+"F0.wireOp",EDGE,"E10.0.1.2"),sQuery(id+"F0.wireOp",EDGE,"E10.0.1.3"),sQuery(id+"F0.wireOp",EDGE,"E10.0.1.4"),sQuery(id+"F0.wireOp",EDGE,"E10.0.1.5"),sQuery(id+"F0.wireOp",EDGE,"E10.0.1.6"),sQuery(id+"F0.wireOp",EDGE,"E10.0.1.9"),sQuery(id+"F0.wireOp",EDGE,"E10.0.1.10"),sQuery(id+"F0.wireOp",EDGE,"E10.0.1.11"),sQuery(id+"F0.wireOp",EDGE,"E10.0.2.2"),sQuery(id+"F0.wireOp",EDGE,"E10.0.2.3"),sQuery(id+"F0.wireOp",EDGE,"E10.0.2.4"),sQuery(id+"F0.wireOp",EDGE,"E10.0.2.5"),sQuery(id+"F0.wireOp",EDGE,"E10.0.2.6"),sQuery(id+"F0.wireOp",EDGE,"E10.0.2.9"),sQuery(id+"F0.wireOp",EDGE,"E10.0.2.10"),sQuery(id+"F0.wireOp",EDGE,"E10.0.2.11"),sQuery(id+"F0.wireOp",EDGE,"E10.0.3.2"),sQuery(id+"F0.wireOp",EDGE,"E10.0.3.3"),sQuery(id+"F0.wireOp",EDGE,"E10.0.3.4"),sQuery(id+"F0.wireOp",EDGE,"E10.0.3.5"),sQuery(id+"F0.wireOp",EDGE,"E10.0.3.6"),sQuery(id+"F0.wireOp",EDGE,"E10.0.3.9"),sQuery(id+"F0.wireOp",EDGE,"E10.0.3.10"),sQuery(id+"F0.wireOp",EDGE,"E10.0.3.11"),sQuery(id+"F0.wireOp",EDGE,"E10.0.4.2"),sQuery(id+"F0.wireOp",EDGE,"E10.0.4.3"),sQuery(id+"F0.wireOp",EDGE,"E10.0.4.4"),sQuery(id+"F0.wireOp",EDGE,"E10.0.4.5"),sQuery(id+"F0.wireOp",EDGE,"E10.0.4.6"),sQuery(id+"F0.wireOp",EDGE,"E10.0.4.9"),sQuery(id+"F0.wireOp",EDGE,"E10.0.4.10"),sQuery(id+"F0.wireOp",EDGE,"E10.0.4.11"),sQuery(id+"F0.wireOp",EDGE,"E10.0.5.2"),sQuery(id+"F0.wireOp",EDGE,"E10.0.5.3"),sQuery(id+"F0.wireOp",EDGE,"E10.0.5.4"),sQuery(id+"F0.wireOp",EDGE,"E10.0.5.5"),sQuery(id+"F0.wireOp",EDGE,"E10.0.5.6"),sQuery(id+"F0.wireOp",EDGE,"E10.0.5.9"),sQuery(id+"F0.wireOp",EDGE,"E10.0.5.10"),sQuery(id+"F0.wireOp",EDGE,"E10.0.5.11"),sQuery(id+"F0.wireOp",EDGE,"E10.0.6.2"),sQuery(id+"F0.wireOp",EDGE,"E10.0.6.3"),sQuery(id+"F0.wireOp",EDGE,"E10.0.6.4"),sQuery(id+"F0.wireOp",EDGE,"E10.0.6.5"),sQuery(id+"F0.wireOp",EDGE,"E10.0.6.6"),sQuery(id+"F0.wireOp",EDGE,"E10.0.6.9"),sQuery(id+"F0.wireOp",EDGE,"E10.0.6.10"),sQuery(id+"F0.wireOp",EDGE,"E10.0.6.11"),sQuery(id+"F0.wireOp",EDGE,"E10.0.7.2"),sQuery(id+"F0.wireOp",EDGE,"E10.0.7.3"),sQuery(id+"F0.wireOp",EDGE,"E10.0.7.4"),sQuery(id+"F0.wireOp",EDGE,"E10.0.7.5"),sQuery(id+"F0.wireOp",EDGE,"E10.0.7.6"),sQuery(id+"F0.wireOp",EDGE,"E10.0.7.9"),sQuery(id+"F0.wireOp",EDGE,"E10.0.7.10"),sQuery(id+"F0.wireOp",EDGE,"E10.0.7.11"),sQuery(id+"F0.wireOp",EDGE,"E10.0.8.2"),sQuery(id+"F0.wireOp",EDGE,"E10.0.8.3"),sQuery(id+"F0.wireOp",EDGE,"E10.0.8.4"),sQuery(id+"F0.wireOp",EDGE,"E10.0.8.5"),sQuery(id+"F0.wireOp",EDGE,"E10.0.8.6"),sQuery(id+"F0.wireOp",EDGE,"E10.0.8.9"),sQuery(id+"F0.wireOp",EDGE,"E10.0.8.10"),sQuery(id+"F0.wireOp",EDGE,"E10.0.8.11"),sQuery(id+"F0.wireOp",EDGE,"E10.0.9.2"),sQuery(id+"F0.wireOp",EDGE,"E10.0.9.3"),sQuery(id+"F0.wireOp",EDGE,"E10.0.9.4"),sQuery(id+"F0.wireOp",EDGE,"E10.0.9.5"),sQuery(id+"F0.wireOp",EDGE,"E10.0.9.6"),sQuery(id+"F0.wireOp",EDGE,"E10.0.9.9"),sQuery(id+"F0.wireOp",EDGE,"E10.0.9.10"),sQuery(id+"F0.wireOp",EDGE,"E10.0.9.11"),sQuery(id+"F0.wireOp",EDGE,"E10.0.10.2"),sQuery(id+"F0.wireOp",EDGE,"E10.0.10.3"),sQuery(id+"F0.wireOp",EDGE,"E10.0.10.4"),sQuery(id+"F0.wireOp",EDGE,"E10.0.10.5"),sQuery(id+"F0.wireOp",EDGE,"E10.0.10.6"),sQuery(id+"F0.wireOp",EDGE,"E10.0.10.9"),sQuery(id+"F0.wireOp",EDGE,"E10.0.10.10"),sQuery(id+"F0.wireOp",EDGE,"E10.0.10.11"),sQuery(id+"F0.wireOp",EDGE,"E10.0.11.2"),sQuery(id+"F0.wireOp",EDGE,"E10.0.11.3"),sQuery(id+"F0.wireOp",EDGE,"E10.0.11.4"),sQuery(id+"F0.wireOp",EDGE,"E10.0.11.5"),sQuery(id+"F0.wireOp",EDGE,"E10.0.11.6"),sQuery(id+"F0.wireOp",EDGE,"E10.0.11.9"),sQuery(id+"F0.wireOp",EDGE,"E10.0.11.10"),sQuery(id+"F0.wireOp",EDGE,"E10.0.11.11"),sQuery(id+"F0.wireOp",EDGE,"E10.0.12.2"),sQuery(id+"F0.wireOp",EDGE,"E10.0.12.3"),sQuery(id+"F0.wireOp",EDGE,"E10.0.12.4"),sQuery(id+"F0.wireOp",EDGE,"E10.0.12.5"),sQuery(id+"F0.wireOp",EDGE,"E10.0.12.6"),sQuery(id+"F0.wireOp",EDGE,"E10.0.12.9"),sQuery(id+"F0.wireOp",EDGE,"E10.0.12.10"),sQuery(id+"F0.wireOp",EDGE,"E10.0.12.11"),sQuery(id+"F0.wireOp",EDGE,"E10.0.13.2"),sQuery(id+"F0.wireOp",EDGE,"E10.0.13.3"),sQuery(id+"F0.wireOp",EDGE,"E10.0.13.4"),sQuery(id+"F0.wireOp",EDGE,"E10.0.13.5"),sQuery(id+"F0.wireOp",EDGE,"E10.0.13.6"),sQuery(id+"F0.wireOp",EDGE,"E10.0.13.9"),sQuery(id+"F0.wireOp",EDGE,"E10.0.13.10"),sQuery(id+"F0.wireOp",EDGE,"E10.0.13.11"),sQuery(id+"F0.wireOp",EDGE,"E10.0.14.2"),sQuery(id+"F0.wireOp",EDGE,"E10.0.14.3"),sQuery(id+"F0.wireOp",EDGE,"E10.0.14.4"),sQuery(id+"F0.wireOp",EDGE,"E10.0.14.5"),sQuery(id+"F0.wireOp",EDGE,"E10.0.14.6"),sQuery(id+"F0.wireOp",EDGE,"E10.0.14.9"),sQuery(id+"F0.wireOp",EDGE,"E10.0.14.10"),sQuery(id+"F0.wireOp",EDGE,"E10.0.14.11"),sQuery(id+"F0.wireOp",EDGE,"E10.0.15.2"),sQuery(id+"F0.wireOp",EDGE,"E10.0.15.3"),sQuery(id+"F0.wireOp",EDGE,"E10.0.15.4"),sQuery(id+"F0.wireOp",EDGE,"E10.0.15.5"),sQuery(id+"F0.wireOp",EDGE,"E10.0.15.6"),sQuery(id+"F0.wireOp",EDGE,"E10.0.15.9"),sQuery(id+"F0.wireOp",EDGE,"E10.0.15.10"),sQuery(id+"F0.wireOp",EDGE,"E10.0.15.11"),sQuery(id+"F0.wireOp",EDGE,"E12.bottom"),sQuery(id+"F0.wireOp",EDGE,"E12.top"),sQuery(id+"F0.wireOp",EDGE,"E12.left"),sQuery(id+"F0.wireOp",EDGE,"E12.right"),sQuery(id+"F0.wireOp",EDGE,"E13.0.1.0"),sQuery(id+"F0.wireOp",EDGE,"E13.0.1.1"),sQuery(id+"F0.wireOp",EDGE,"E13.0.1.2"),sQuery(id+"F0.wireOp",EDGE,"E13.0.1.4"),sQuery(id+"F0.wireOp",EDGE,"E13.0.2.0"),sQuery(id+"F0.wireOp",EDGE,"E13.0.2.1"),sQuery(id+"F0.wireOp",EDGE,"E13.0.2.2"),sQuery(id+"F0.wireOp",EDGE,"E13.0.2.4"),sQuery(id+"F0.wireOp",EDGE,"E13.0.3.0"),sQuery(id+"F0.wireOp",EDGE,"E13.0.3.1"),sQuery(id+"F0.wireOp",EDGE,"E13.0.3.2"),sQuery(id+"F0.wireOp",EDGE,"E13.0.3.4"),sQuery(id+"F0.wireOp",EDGE,"E13.0.4.0"),sQuery(id+"F0.wireOp",EDGE,"E13.0.4.1"),sQuery(id+"F0.wireOp",EDGE,"E13.0.4.2"),sQuery(id+"F0.wireOp",EDGE,"E13.0.4.4"),sQuery(id+"F0.wireOp",EDGE,"E13.0.5.0"),sQuery(id+"F0.wireOp",EDGE,"E13.0.5.1"),sQuery(id+"F0.wireOp",EDGE,"E13.0.5.2"),sQuery(id+"F0.wireOp",EDGE,"E13.0.5.4"),sQuery(id+"F0.wireOp",EDGE,"E13.0.6.0"),sQuery(id+"F0.wireOp",EDGE,"E13.0.6.1"),sQuery(id+"F0.wireOp",EDGE,"E13.0.6.2"),sQuery(id+"F0.wireOp",EDGE,"E13.0.6.4"),sQuery(id+"F0.wireOp",EDGE,"E13.0.7.0"),sQuery(id+"F0.wireOp",EDGE,"E13.0.7.1"),sQuery(id+"F0.wireOp",EDGE,"E13.0.7.2"),sQuery(id+"F0.wireOp",EDGE,"E13.0.7.4"),sQuery(id+"F0.wireOp",EDGE,"E13.0.8.0"),sQuery(id+"F0.wireOp",EDGE,"E13.0.8.1"),sQuery(id+"F0.wireOp",EDGE,"E13.0.8.2"),sQuery(id+"F0.wireOp",EDGE,"E13.0.8.4"),sQuery(id+"F0.wireOp",EDGE,"E13.0.9.0"),sQuery(id+"F0.wireOp",EDGE,"E13.0.9.1"),sQuery(id+"F0.wireOp",EDGE,"E13.0.9.2"),sQuery(id+"F0.wireOp",EDGE,"E13.0.9.4"),sQuery(id+"F0.wireOp",EDGE,"E13.0.10.0"),sQuery(id+"F0.wireOp",EDGE,"E13.0.10.1"),sQuery(id+"F0.wireOp",EDGE,"E13.0.10.2"),sQuery(id+"F0.wireOp",EDGE,"E13.0.10.4"),sQuery(id+"F0.wireOp",EDGE,"E13.0.11.0"),sQuery(id+"F0.wireOp",EDGE,"E13.0.11.1"),sQuery(id+"F0.wireOp",EDGE,"E13.0.11.2"),sQuery(id+"F0.wireOp",EDGE,"E13.0.11.4"),sQuery(id+"F0.wireOp",EDGE,"E13.0.12.0"),sQuery(id+"F0.wireOp",EDGE,"E13.0.12.1"),sQuery(id+"F0.wireOp",EDGE,"E13.0.12.2"),sQuery(id+"F0.wireOp",EDGE,"E13.0.12.4"),sQuery(id+"F0.wireOp",EDGE,"E13.0.13.0"),sQuery(id+"F0.wireOp",EDGE,"E13.0.13.1"),sQuery(id+"F0.wireOp",EDGE,"E13.0.13.2"),sQuery(id+"F0.wireOp",EDGE,"E13.0.13.4"),sQuery(id+"F0.wireOp",EDGE,"E13.0.14.0"),sQuery(id+"F0.wireOp",EDGE,"E13.0.14.1"),sQuery(id+"F0.wireOp",EDGE,"E13.0.14.2"),sQuery(id+"F0.wireOp",EDGE,"E13.0.14.4")])]});
            var Q1;
            Q1=makeQuery(id+"F1.opExtrude","SWEPT_FACE",FACE,{"disambiguationData":[OSD([sQuery(id+"F0.wireOp",EDGE,"E0.left")])]});
            mirror(context, id + "F2", {"operationType" : NewBodyOperationType.ADD, "entities" : qUnion([Q0]), "mirrorPlane" : qUnion([Q1])});
        }
    });
